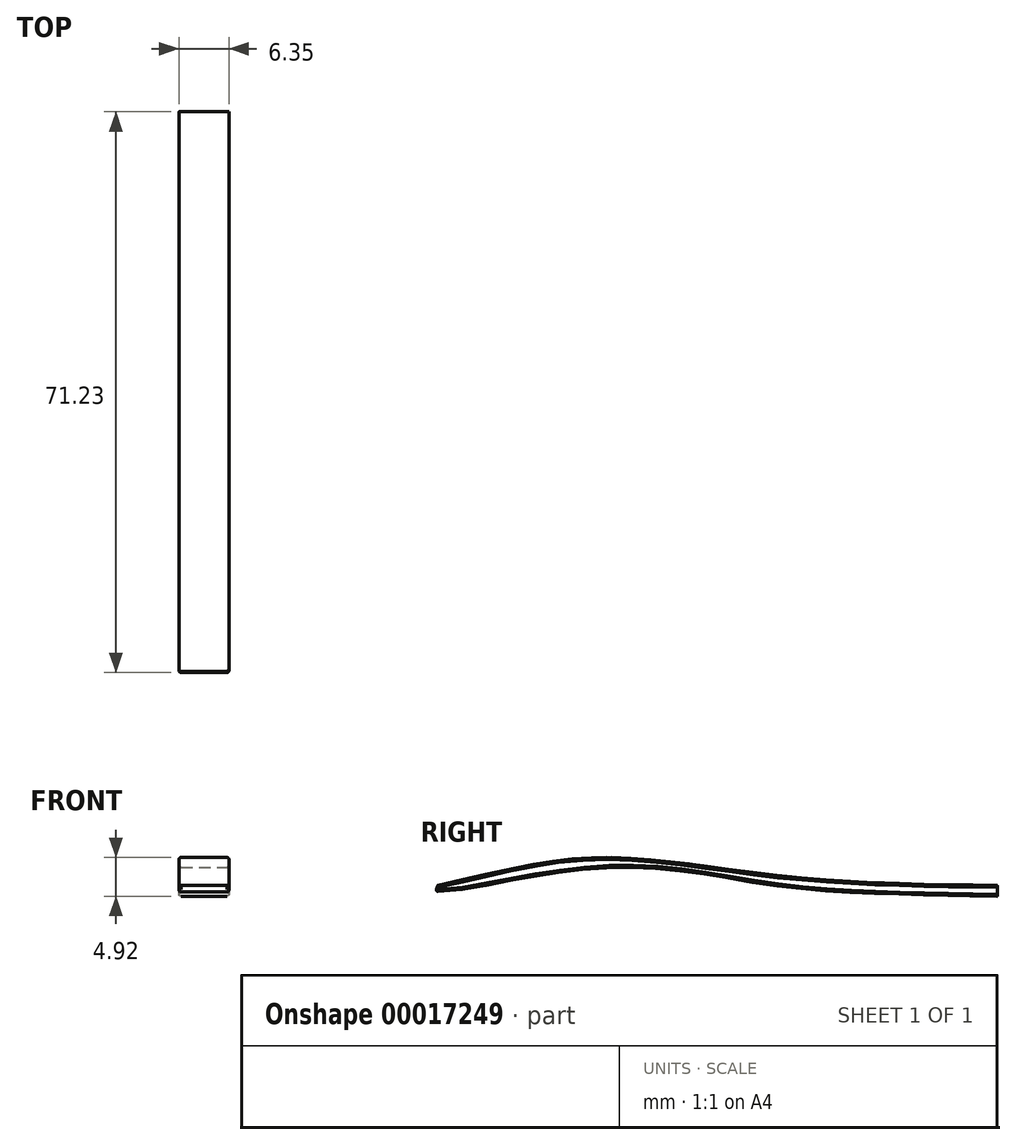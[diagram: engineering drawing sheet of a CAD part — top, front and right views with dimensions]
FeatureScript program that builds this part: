
annotation { "Feature Type Name" : "Feature", "Feature Type Description" : "" }
export const myFeature = defineFeature(function(context is Context, id is Id, definition is map)
    precondition{}
    {
        {
            var Q0;
            Q0=qCreatedBy(makeId("Right.planeOp"),FACE);
            var sketch = newSketch(context, id + "F0", { "sketchPlane" : qUnion([Q0])});
            skFitSpline(sketch, "E0", {"points": [v(-42.73, 0) * mm, v(-22.59, 3.54) * mm, v(0, 1.29) * mm, v(28.34, 0) * mm], "startDerivative": vector(74.02, 16.09) * mm, "endDerivative": vector(86.93, -0.98) * mm});
            skFitSpline(sketch, "E1", {"points": [v(-42.73, 0) * mm, v(-42.73, -0.77) * mm, v(-22.59, 2.18) * mm, v(0, 0) * mm, v(28.34, -1.37) * mm], "startDerivative": vector(-9.07, -23.67) * mm, "endDerivative": vector(97.1, -1.95) * mm});
            skLineSegment(sketch, "E2", {"start": v(28.34, 0) * mm, "end": v(28.34, -1.37) * mm});
            skSolve(sketch);
        }
        {
            var Q0;
            Q0=makeQuery(id+"F0.imprint","IMPRINT",FACE,{"disambiguationData":[TD([[makeQuery(id+"F0.imprint","IMPRINT",EDGE,{"derivedFrom":sQuery(id+"F0.wireOp",EDGE,"E0")}),-1.0]])]});
            extrude(context, id + "F1", {"entities" : qUnion([Q0]), "oppositeDirection" : true, "depth" : 6.35 * mm});
        }
        {
            var Q0;
            Q0=makeQuery(id+"F1.opExtrude","CAP_EDGE",EDGE,{"disambiguationData":[OSD([sQuery(id+"F0.wireOp",EDGE,"E0")])],"isStart":true});
            var Q1;
            Q1=makeQuery(id+"F1.opExtrude","CAP_EDGE",EDGE,{"disambiguationData":[OSD([sQuery(id+"F0.wireOp",EDGE,"E1")])],"isStart":true});
            var Q2;
            Q2=makeQuery(id+"F1.opExtrude","CAP_EDGE",EDGE,{"disambiguationData":[OSD([sQuery(id+"F0.wireOp",EDGE,"E1")])],"isStart":false});
            var Q3;
            Q3=makeQuery(id+"F1.opExtrude","CAP_EDGE",EDGE,{"disambiguationData":[OSD([sQuery(id+"F0.wireOp",EDGE,"E0")])],"isStart":false});
            fillet(context, id + "F2", {"entities" : qUnion([Q0, Q1, Q2, Q3]), "radius" : 0.25 * mm, "tangentPropagation" : true, "allowEdgeOverflow" : false});
        }
    });
